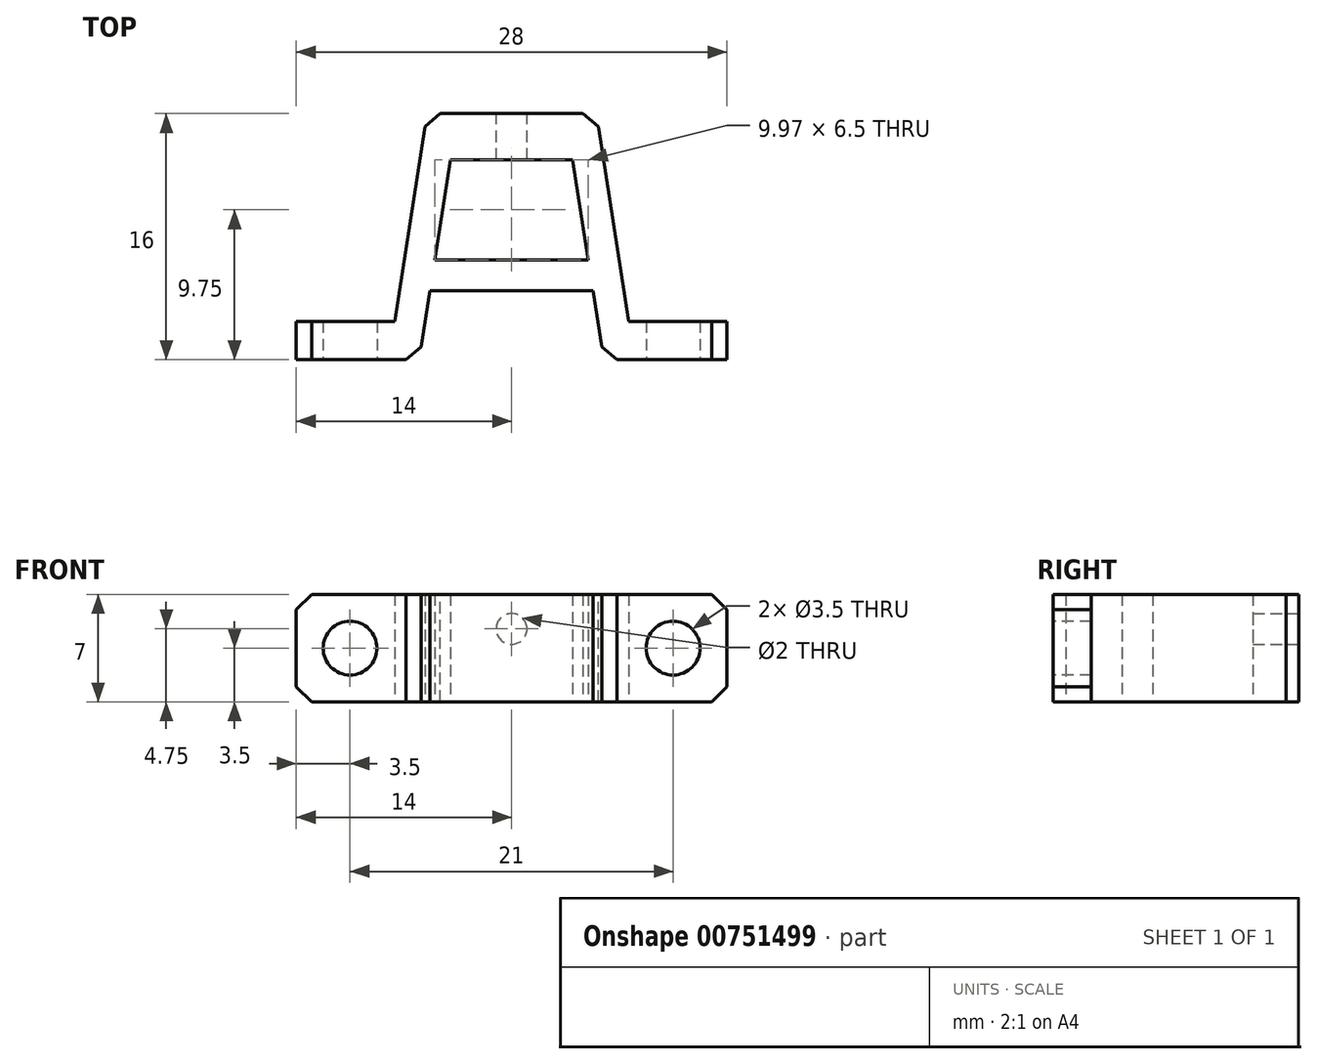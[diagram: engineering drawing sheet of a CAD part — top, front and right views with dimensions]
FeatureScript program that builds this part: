
annotation { "Feature Type Name" : "Feature", "Feature Type Description" : "" }
export const myFeature = defineFeature(function(context is Context, id is Id, definition is map)
    precondition{}
    {
        {
            var Q0;
            Q0=qCreatedBy(makeId("Top.planeOp"),FACE);
            var sketch = newSketch(context, id + "F0", { "sketchPlane" : qUnion([Q0])});
            skLineSegment(sketch, "E0.bottom", {"start": v(0, 0) * mm, "end": v(11, 0) * mm});
            skLineSegment(sketch, "E0.top", {"start": v(0, 3) * mm, "end": v(11, 3) * mm});
            skLineSegment(sketch, "E0.left", {"start": v(0, 0) * mm, "end": v(0, 3) * mm});
            skLineSegment(sketch, "E0.right", {"start": v(11, 0) * mm, "end": v(11, 3) * mm});
            skLineSegment(sketch, "E1", {"start": v(0, 3) * mm, "end": v(-2.5, -13) * mm});
            skLineSegment(sketch, "E2", {"start": v(-2.5, -13) * mm, "end": v(-0.5, -13) * mm});
            skLineSegment(sketch, "E3", {"start": v(11, 3) * mm, "end": v(13.5, -13) * mm});
            skLineSegment(sketch, "E4", {"start": v(13.5, -13) * mm, "end": v(11.5, -13) * mm});
            skLineSegment(sketch, "E5", {"start": v(-0.5, -13) * mm, "end": v(1.53, 0) * mm});
            skLineSegment(sketch, "E6", {"start": v(9.47, 0) * mm, "end": v(11.5, -13) * mm});
            skLineSegment(sketch, "E7", {"start": v(0.52, -6.5) * mm, "end": v(10.48, -6.5) * mm});
            skLineSegment(sketch, "E8", {"start": v(0.2, -8.5) * mm, "end": v(10.8, -8.5) * mm});
            skLineSegment(sketch, "E9", {"start": v(-2.5, -13) * mm, "end": v(-8.5, -13) * mm});
            skLineSegment(sketch, "E10", {"start": v(-8.5, -13) * mm, "end": v(-8.5, -10.5) * mm});
            skLineSegment(sketch, "E11", {"start": v(-8.5, -10.5) * mm, "end": v(-2.1, -10.5) * mm});
            skLineSegment(sketch, "E12", {"start": v(13.5, -13) * mm, "end": v(19.5, -13) * mm});
            skLineSegment(sketch, "E13", {"start": v(19.5, -13) * mm, "end": v(19.5, -10.5) * mm});
            skLineSegment(sketch, "E14", {"start": v(19.5, -10.5) * mm, "end": v(13.1, -10.5) * mm});
            skSolve(sketch);
        }
        {
            var Q0;
            Q0=makeQuery(id+"F0.imprint","IMPRINT",FACE,{"disambiguationData":[TD([[makeQuery(id+"F0.imprint","IMPRINT",EDGE,{"derivedFrom":sQuery(id+"F0.wireOp",EDGE,"E0.top")}),-1.0]])]});
            var Q1;
            {var subQ3=sQuery(id+"F0.wireOp",EDGE,"E0.left");Q1=makeQuery(id+"F0.imprint","IMPRINT",FACE,{"disambiguationData":[TD([[makeQuery(id+"F0.imprint","IMPRINT",EDGE,{"derivedFrom":subQ3}),1.0]])]});}
            var Q2;
            {var subQ0=sQuery(id+"F0.wireOp",EDGE,"E7");Q2=makeQuery(id+"F0.imprint","IMPRINT",FACE,{"disambiguationData":[TD([[makeQuery(id+"F0.imprint","IMPRINT",EDGE,{"derivedFrom":subQ0}),-1.0]])]});}
            var Q3;
            {var subQ1=sQuery(id+"F0.wireOp",EDGE,"E0.right");Q3=makeQuery(id+"F0.imprint","IMPRINT",FACE,{"disambiguationData":[TD([[makeQuery(id+"F0.imprint","IMPRINT",EDGE,{"derivedFrom":subQ1}),-1.0]])]});}
            var Q4;
            {var subQ0=sQuery(id+"F0.wireOp",EDGE,"E12");Q4=makeQuery(id+"F0.imprint","IMPRINT",FACE,{"disambiguationData":[TD([[makeQuery(id+"F0.imprint","IMPRINT",EDGE,{"derivedFrom":subQ0}),1.0]])]});}
            var Q5;
            {var subQ0=sQuery(id+"F0.wireOp",EDGE,"E9");Q5=makeQuery(id+"F0.imprint","IMPRINT",FACE,{"disambiguationData":[TD([[makeQuery(id+"F0.imprint","IMPRINT",EDGE,{"derivedFrom":subQ0}),-1.0]])]});}
            extrude(context, id + "F1", {"entities" : qUnion([Q0, Q1, Q2, Q3, Q4, Q5]), "depth" : 7 * mm, "offsetDistance" : 25 * mm});
        }
        {
            var Q0;
            Q0=makeQuery(id+"F1.opExtrude","SWEPT_FACE",FACE,{"disambiguationData":[OSD([sQuery(id+"F0.wireOp",EDGE,"E2"),sQuery(id+"F0.wireOp",EDGE,"E9")])]});
            var sketch = newSketch(context, id + "F2", { "sketchPlane" : qUnion([Q0])});
            skCircle(sketch, "E15", {"center": v(-5, 3.5) * mm, "radius": 1.75 * mm});
            skPoint(sketch, "E15.centerSnap0", {"position": v(-8.5, 3.5) * mm});
            skCircle(sketch, "E16", {"center": v(16, 3.5) * mm, "radius": 1.75 * mm});
            skLineSegment(sketch, "E17", {"start": v(-5, 3.5) * mm, "end": v(-8.5, 3.5) * mm, "construction": true});
            skLineSegment(sketch, "E18", {"start": v(16, 3.5) * mm, "end": v(19.5, 3.5) * mm, "construction": true});
            skSolve(sketch);
        }
        {
            var Q0;
            Q0=makeQuery(id+"F2.imprint","IMPRINT",FACE,{"disambiguationData":[TD([[makeQuery(id+"F2.imprint","IMPRINT",EDGE,{"derivedFrom":sQuery(id+"F2.wireOp",EDGE,"E15")}),1.0]])]});
            var Q1;
            Q1=makeQuery(id+"F2.imprint","IMPRINT",FACE,{"disambiguationData":[TD([[makeQuery(id+"F2.imprint","IMPRINT",EDGE,{"derivedFrom":sQuery(id+"F2.wireOp",EDGE,"E16")}),1.0]])]});
            var Q2;
            Q2=makeQuery(id+"F1.opExtrude","SWEPT_FACE",FACE,{"disambiguationData":[OSD([sQuery(id+"F0.wireOp",EDGE,"E14")])]});
            extrude(context, id + "F3", {"entities" : qUnion([Q0, Q1]), "operationType" : NewBodyOperationType.REMOVE, "endBound" : BoundingType.UP_TO_SURFACE, "oppositeDirection" : true, "depth" : 25 * mm, "endBoundEntityFace" : qUnion([Q2]), "offsetDistance" : 25 * mm});
        }
        {
            var Q0;
            Q0=makeQuery(id+"F1.opExtrude","SWEPT_FACE",FACE,{"disambiguationData":[OSD([sQuery(id+"F0.wireOp",EDGE,"E0.top")])]});
            var sketch = newSketch(context, id + "F4", { "sketchPlane" : qUnion([Q0])});
            skCircle(sketch, "E19", {"center": v(-5.5, 4.75) * mm, "radius": 1 * mm});
            skSolve(sketch);
        }
        {
            var Q0;
            Q0=makeQuery(id+"F4.imprint","IMPRINT",FACE,{"disambiguationData":[TD([[makeQuery(id+"F4.imprint","IMPRINT",EDGE,{"derivedFrom":sQuery(id+"F4.wireOp",EDGE,"E19")}),1.0]])]});
            var Q1;
            Q1=makeQuery(id+"F1.opExtrude","SWEPT_FACE",FACE,{"disambiguationData":[OSD([sQuery(id+"F0.wireOp",EDGE,"E0.bottom")])]});
            extrude(context, id + "F5", {"entities" : qUnion([Q0]), "operationType" : NewBodyOperationType.REMOVE, "endBound" : BoundingType.UP_TO_SURFACE, "oppositeDirection" : true, "depth" : 25 * mm, "endBoundEntityFace" : qUnion([Q1]), "offsetDistance" : 25 * mm});
        }
        {
            var Q0;
            Q0=makeQuery(id+"F1.opExtrude","CAP_EDGE",EDGE,{"disambiguationData":[OSD([sQuery(id+"F0.wireOp",EDGE,"E10")])],"isStart":false});
            var Q1;
            Q1=makeQuery(id+"F1.opExtrude","CAP_EDGE",EDGE,{"disambiguationData":[OSD([sQuery(id+"F0.wireOp",EDGE,"E10")])],"isStart":true});
            var Q2;
            Q2=makeQuery(id+"F1.opExtrude","CAP_EDGE",EDGE,{"disambiguationData":[OSD([sQuery(id+"F0.wireOp",EDGE,"E13")])],"isStart":false});
            var Q3;
            Q3=makeQuery(id+"F1.opExtrude","CAP_EDGE",EDGE,{"disambiguationData":[OSD([sQuery(id+"F0.wireOp",EDGE,"E13")])],"isStart":true});
            var Q4;
            Q4=makeQuery(id+"F1.opExtrude","SWEPT_EDGE",EDGE,{"disambiguationData":[OSD([sQuery(id+"F0.wireOp",EDGE,"E0.top"),sQuery(id+"F0.wireOp",EDGE,"E0.left"),sQuery(id+"F0.wireOp",EDGE,"E1")])]});
            var Q5;
            Q5=makeQuery(id+"F1.opExtrude","SWEPT_EDGE",EDGE,{"disambiguationData":[OSD([sQuery(id+"F0.wireOp",EDGE,"E0.top"),sQuery(id+"F0.wireOp",EDGE,"E0.right"),sQuery(id+"F0.wireOp",EDGE,"E3")])]});
            var Q6;
            Q6=makeQuery(id+"F1.opExtrude","SWEPT_EDGE",EDGE,{"disambiguationData":[OSD([sQuery(id+"F0.wireOp",EDGE,"E2"),sQuery(id+"F0.wireOp",EDGE,"E5")])]});
            var Q7;
            Q7=makeQuery(id+"F1.opExtrude","SWEPT_EDGE",EDGE,{"disambiguationData":[OSD([sQuery(id+"F0.wireOp",EDGE,"E4"),sQuery(id+"F0.wireOp",EDGE,"E6")])]});
            chamfer(context, id + "F6", {"entities" : qUnion([Q0, Q1, Q2, Q3, Q4, Q5, Q6, Q7]), "width" : 1 * mm, "tangentPropagation" : true});
        }
    });
